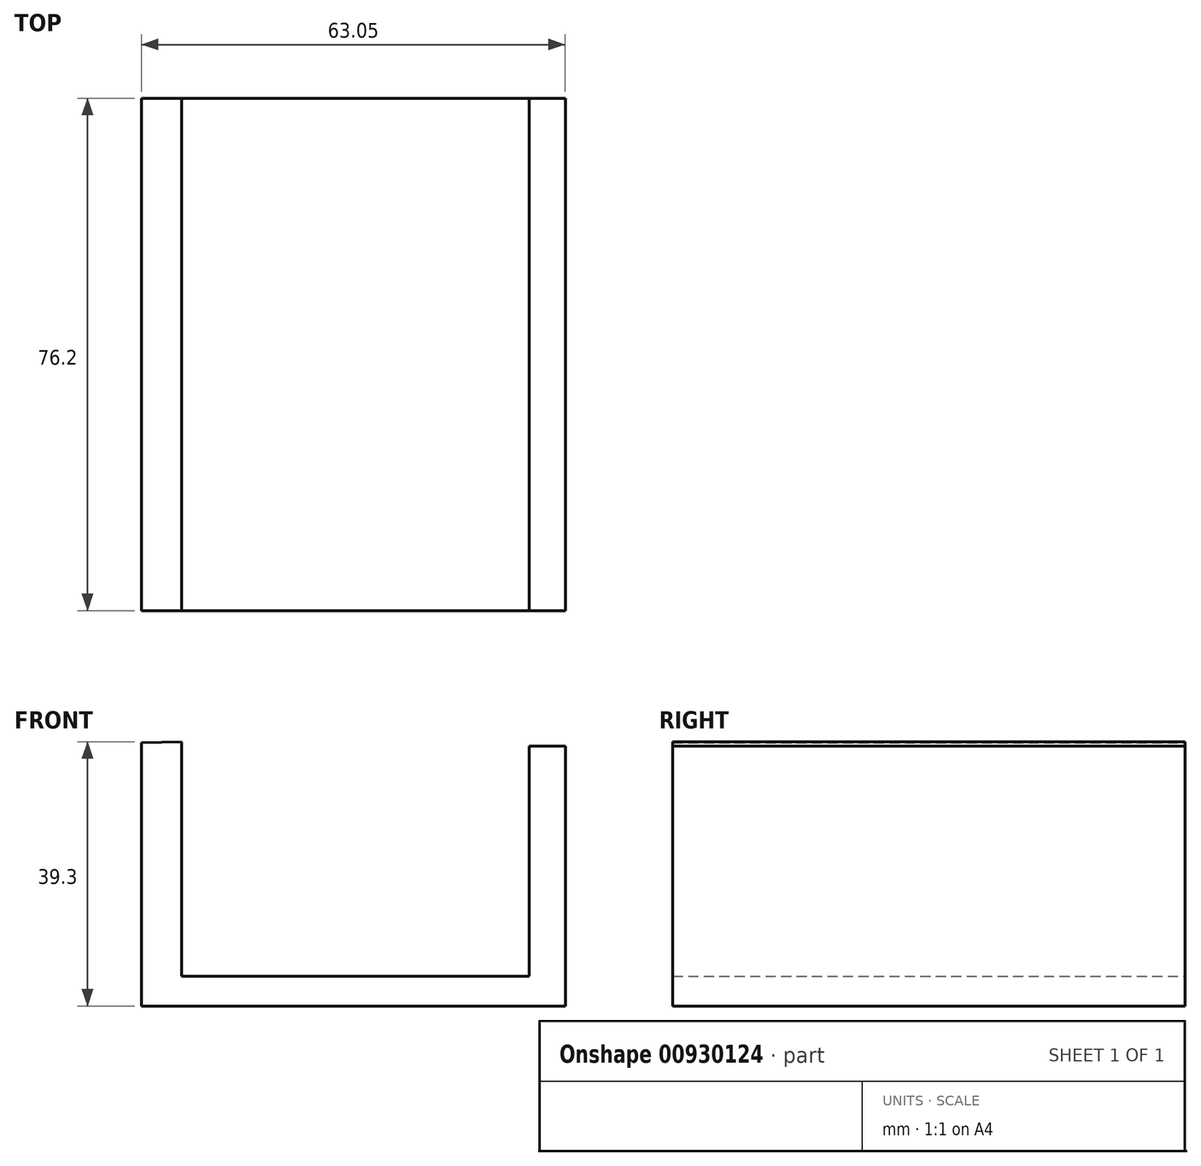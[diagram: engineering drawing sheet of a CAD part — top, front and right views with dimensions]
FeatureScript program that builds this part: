
annotation { "Feature Type Name" : "Feature", "Feature Type Description" : "" }
export const myFeature = defineFeature(function(context is Context, id is Id, definition is map)
    precondition{}
    {
        {
            var Q0;
            Q0=qCreatedBy(makeId("Front.planeOp"),FACE);
            var sketch = newSketch(context, id + "F0", { "sketchPlane" : qUnion([Q0])});
            skLineSegment(sketch, "E0", {"start": v(-35.01, 39.15) * mm, "end": v(-35.01, 0) * mm});
            skLineSegment(sketch, "E1", {"start": v(-35.01, 0) * mm, "end": v(28.04, 0) * mm});
            skLineSegment(sketch, "E2", {"start": v(28.04, 0) * mm, "end": v(28.04, 38.66) * mm});
            skLineSegment(sketch, "E3", {"start": v(28.04, 38.66) * mm, "end": v(22.66, 38.66) * mm});
            skLineSegment(sketch, "E4", {"start": v(22.66, 38.66) * mm, "end": v(22.66, 4.44) * mm});
            skLineSegment(sketch, "E5", {"start": v(22.66, 4.44) * mm, "end": v(-29, 4.44) * mm});
            skLineSegment(sketch, "E6", {"start": v(-29, 4.44) * mm, "end": v(-29, 39.3) * mm});
            skLineSegment(sketch, "E7", {"start": v(-29, 39.3) * mm, "end": v(-35.01, 39.15) * mm});
            skSolve(sketch);
        }
        {
            var Q0;
            Q0 = qSketchRegion(id + "F0", true);
            extrude(context, id + "F1", {"entities" : qUnion([Q0]), "depth" : 76.2 * mm, "offsetDistance" : 25.4 * mm});
        }
    });
